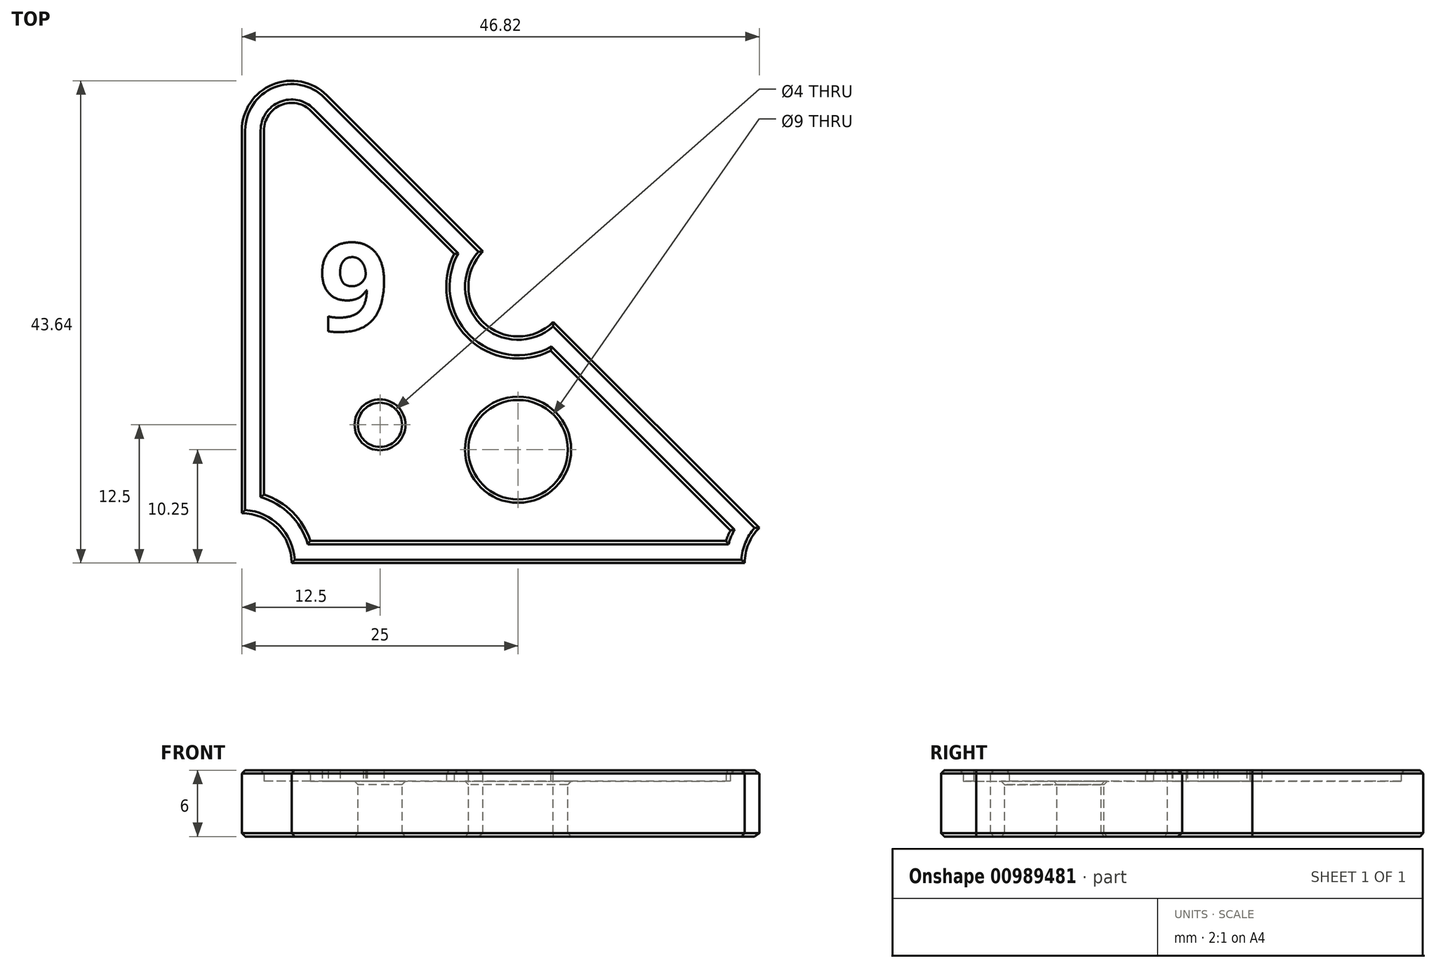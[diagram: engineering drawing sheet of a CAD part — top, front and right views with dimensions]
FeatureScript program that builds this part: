
annotation { "Feature Type Name" : "Feature", "Feature Type Description" : "" }
export const myFeature = defineFeature(function(context is Context, id is Id, definition is map)
    precondition{}
    {
        {
            var Q0;
            Q0=qCreatedBy(makeId("Top.planeOp"),FACE);
            var sketch = newSketch(context, id + "F0", { "sketchPlane" : qUnion([Q0])});
            skLineSegment(sketch, "E0", {"start": v(-25, 25) * mm, "end": v(-25, -25) * mm});
            skLineSegment(sketch, "E1", {"start": v(-25, -25) * mm, "end": v(25, -25) * mm});
            skLineSegment(sketch, "E2", {"start": v(25, -25) * mm, "end": v(-25, 25) * mm});
            skPoint(sketch, "E3", {"position": v(0, 0) * mm});
            skCircle(sketch, "E4", {"center": v(-25, -25) * mm, "radius": 4.5 * mm});
            skCircle(sketch, "E5", {"center": v(25, -25) * mm, "radius": 4.5 * mm});
            skCircle(sketch, "E6", {"center": v(0, 0) * mm, "radius": 4.5 * mm});
            skArc(sketch, "E7", {"start": v(-17.32, 17.32) * mm, "mid": v(-22.22, 18.3) * mm, "end": v(-25, 14.14) * mm});
            skCircle(sketch, "E8", {"center": v(-12.5, -12.5) * mm, "radius": 2 * mm});
            skLineSegment(sketch, "E9", {"start": v(0, 0) * mm, "end": v(-25, -25) * mm, "construction": true});
            skCircle(sketch, "E10", {"center": v(0, -14.75) * mm, "radius": 4.5 * mm});
            skLineSegment(sketch, "E11", {"start": v(0, -4.5) * mm, "end": v(0, -25) * mm, "construction": true});
            skPoint(sketch, "E11.startSnap0", {"position": v(0, -25) * mm});
            skLineSegment(sketch, "E12", {"start": v(-4.5, 4.5) * mm, "end": v(-4.5, -6.56) * mm, "construction": true});
            skLineSegment(sketch, "E13", {"start": v(-4.5, 0) * mm, "end": v(-25, 0) * mm, "construction": true});
            skText(sketch, "E14", { "text": "9", "fontName": "OpenSans-Bold.ttf"});
            skPoint(sketch, "E15", {"position": v(-14.75, 0) * mm});
            const initialGuessF0  = {"E14": [-0.01809, -0.004, 1, 0, 0.008]};
            skSetInitialGuess(sketch, initialGuessF0);
            skSolve(sketch);
        }
        {
            var Q0;
            {var subQ5=sQuery(id+"F0.wireOp",EDGE,"E7");Q0=makeQuery(id+"F0.imprint","IMPRINT",FACE,{"disambiguationData":[TD([[makeQuery(id+"F0.imprint","IMPRINT",EDGE,{"derivedFrom":subQ5}),1.0]])]});}
            var Q1;
            Q1=makeQuery(id+"F0.imprint","IMPRINT",FACE,{"disambiguationData":[TD([[makeQuery(id+"F0.imprint","IMPRINT",EDGE,{"derivedFrom":sQuery(id+"F0.wireOp",EDGE,"E14.sketch_text.stroke-0")}),-1.0]])]});
            var Q2;
            Q2=makeQuery(id+"F0.imprint","IMPRINT",FACE,{"disambiguationData":[TD([[makeQuery(id+"F0.imprint","IMPRINT",EDGE,{"derivedFrom":sQuery(id+"F0.wireOp",EDGE,"E14.sketch_text.stroke-18")}),1.0]])]});
            extrude(context, id + "F1", {"entities" : qUnion([Q0, Q1, Q2]), "oppositeDirection" : true, "depth" : 5 * mm, "offsetDistance" : 25 * mm});
        }
        {
            var Q0;
            Q0=makeQuery(id+"F1.opExtrude","CAP_FACE",FACE,{"disambiguationData":[OSD([sQuery(id+"F0.wireOp",EDGE,"E0"),sQuery(id+"F0.wireOp",EDGE,"E1"),sQuery(id+"F0.wireOp",EDGE,"E2"),sQuery(id+"F0.wireOp",EDGE,"E4"),sQuery(id+"F0.wireOp",EDGE,"E5"),sQuery(id+"F0.wireOp",EDGE,"E6"),sQuery(id+"F0.wireOp",EDGE,"E7"),sQuery(id+"F0.wireOp",EDGE,"E8"),sQuery(id+"F0.wireOp",EDGE,"E10")])],"isStart":true});
            var sketch = newSketch(context, id + "F2", { "sketchPlane" : qUnion([Q0])});
            skLineSegment(sketch, "E16.0", {"start": v(19.21, -22.04) * mm, "end": v(2.96, -5.79) * mm});
            skArc(sketch, "E16.1", {"start": v(18.82, -23) * mm, "mid": v(19, -22.51) * mm, "end": v(19.21, -22.04) * mm});
            skArc(sketch, "E16.2", {"start": v(2.96, -5.79) * mm, "mid": v(-4.6, -4.6) * mm, "end": v(-5.79, 2.96) * mm});
            skLineSegment(sketch, "E16.3", {"start": v(-18.82, -23) * mm, "end": v(18.82, -23) * mm});
            skLineSegment(sketch, "E16.4", {"start": v(-5.79, 2.96) * mm, "end": v(-18.73, 15.9) * mm});
            skArc(sketch, "E16.5", {"start": v(-18.73, 15.9) * mm, "mid": v(-21.46, 16.45) * mm, "end": v(-23, 14.14) * mm});
            skLineSegment(sketch, "E16.6", {"start": v(-23, 14.14) * mm, "end": v(-23, -18.82) * mm});
            skArc(sketch, "E16.7", {"start": v(-23, -18.82) * mm, "mid": v(-20.4, -20.4) * mm, "end": v(-18.82, -23) * mm});
            skSolve(sketch);
        }
        {
            var Q0;
            Q0=makeQuery(id+"F0.imprint","IMPRINT",FACE,{"disambiguationData":[TD([[makeQuery(id+"F0.imprint","IMPRINT",EDGE,{"derivedFrom":sQuery(id+"F0.wireOp",EDGE,"E14.sketch_text.stroke-0")}),-1.0]])]});
            var Q1;
            Q1=makeQuery(id+"F2.imprint","IMPRINT",FACE,{"disambiguationData":[TD([[makeQuery(id+"F2.imprint","IMPRINT",EDGE,{"derivedFrom":sQuery(id+"F2.wireOp",EDGE,"E16.0")}),-1.0]])]});
            extrude(context, id + "F3", {"entities" : qUnion([Q0, Q1]), "operationType" : NewBodyOperationType.ADD, "depth" : 1 * mm, "offsetDistance" : 25 * mm});
        }
        {
            var Q0;
            Q0=makeQuery(id+"F1.opExtrude","CAP_EDGE",EDGE,{"disambiguationData":[OSD([sQuery(id+"F0.wireOp",EDGE,"E8")])],"isStart":true});
            var Q1;
            Q1=makeQuery(id+"F1.opExtrude","CAP_EDGE",EDGE,{"disambiguationData":[OSD([sQuery(id+"F0.wireOp",EDGE,"E10")])],"isStart":true});
            var Q2;
            Q2=makeQuery(id+"F3.opExtrude","CAP_FACE",FACE,{"disambiguationData":[OSD([sQuery(id+"F0.wireOp",EDGE,"E0"),sQuery(id+"F0.wireOp",EDGE,"E1"),sQuery(id+"F0.wireOp",EDGE,"E2"),sQuery(id+"F0.wireOp",EDGE,"E4"),sQuery(id+"F0.wireOp",EDGE,"E5"),sQuery(id+"F0.wireOp",EDGE,"E6"),sQuery(id+"F0.wireOp",EDGE,"E7"),sQuery(id+"F2.wireOp",EDGE,"E16.0"),sQuery(id+"F2.wireOp",EDGE,"E16.1"),sQuery(id+"F2.wireOp",EDGE,"E16.2"),sQuery(id+"F2.wireOp",EDGE,"E16.3"),sQuery(id+"F2.wireOp",EDGE,"E16.4"),sQuery(id+"F2.wireOp",EDGE,"E16.5"),sQuery(id+"F2.wireOp",EDGE,"E16.6"),sQuery(id+"F2.wireOp",EDGE,"E16.7")])],"isStart":false});
            var Q3;
            Q3=makeQuery(id+"F1.opExtrude","CAP_FACE",FACE,{"disambiguationData":[OSD([sQuery(id+"F0.wireOp",EDGE,"E0"),sQuery(id+"F0.wireOp",EDGE,"E1"),sQuery(id+"F0.wireOp",EDGE,"E2"),sQuery(id+"F0.wireOp",EDGE,"E4"),sQuery(id+"F0.wireOp",EDGE,"E5"),sQuery(id+"F0.wireOp",EDGE,"E6"),sQuery(id+"F0.wireOp",EDGE,"E7"),sQuery(id+"F0.wireOp",EDGE,"E8"),sQuery(id+"F0.wireOp",EDGE,"E10")])],"isStart":false});
            chamfer(context, id + "F4", {"entities" : qUnion([Q0, Q1, Q2, Q3]), "width" : 0.3 * mm, "tangentPropagation" : true});
        }
    });
